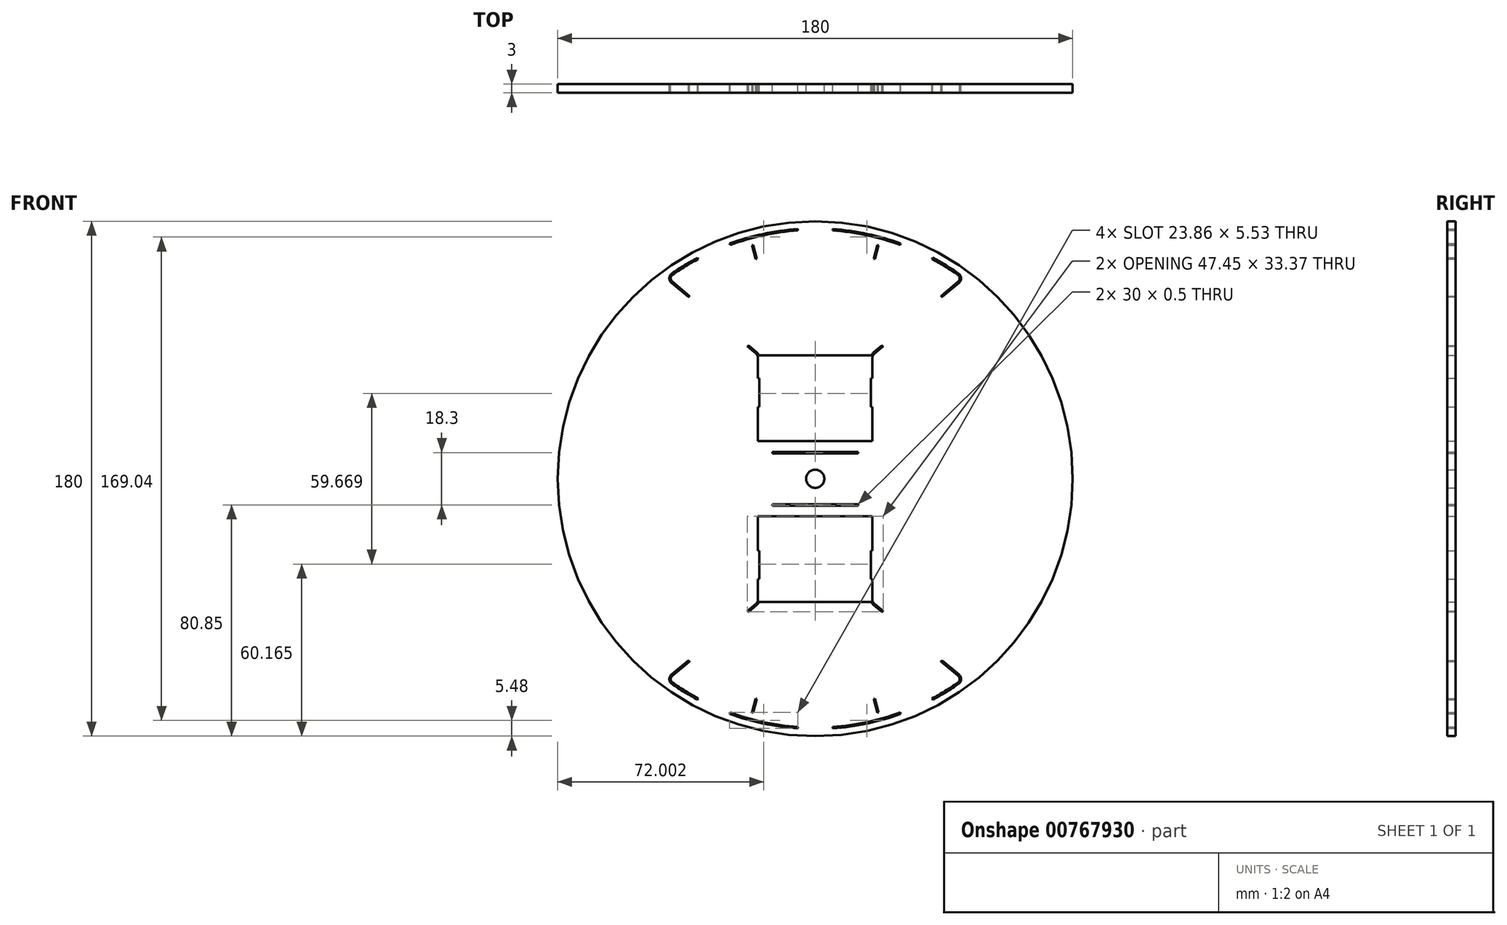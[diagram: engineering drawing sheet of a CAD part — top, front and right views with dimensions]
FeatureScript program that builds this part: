
annotation { "Feature Type Name" : "Feature", "Feature Type Description" : "" }
export const myFeature = defineFeature(function(context is Context, id is Id, definition is map)
    precondition{}
    {
        {
            var Q0;
            Q0=qCreatedBy(makeId("Front.planeOp"),FACE);
            var sketch = newSketch(context, id + "F0", { "sketchPlane" : qUnion([Q0])});
            skCircle(sketch, "E0", {"center": v(0, 0) * mm, "radius": 90 * mm});
            skCircle(sketch, "E1", {"center": v(0, 0) * mm, "radius": 3.17 * mm});
            skLineSegment(sketch, "E2", {"start": v(90, 0) * mm, "end": v(-90, 0) * mm, "construction": true});
            skArc(sketch, "E3", {"start": v(-50.13, -71.72) * mm, "mid": v(-45.69, -74.63) * mm, "end": v(-41.08, -77.26) * mm});
            skLineSegment(sketch, "E4", {"start": v(-20.71, -43.75) * mm, "end": v(-23.72, -46.27) * mm});
            skLineSegment(sketch, "E5", {"start": v(-20, -42.22) * mm, "end": v(-20, -35.15) * mm});
            skLineSegment(sketch, "E6", {"start": v(-18, -13.15) * mm, "end": v(-7.5, -13.15) * mm});
            skLineSegment(sketch, "E7", {"start": v(20, -15.15) * mm, "end": v(20, -25.15) * mm});
            skLineSegment(sketch, "E8.MirrorCS", {"start": v(20.71, -43.75) * mm, "end": v(23.72, -46.27) * mm});
            skPoint(sketch, "E9.visualSharp", {"position": v(-52.23, -70.2) * mm});
            skArc(sketch, "E9.filletArc", {"start": v(-50.27, -68.55) * mm, "mid": v(-50.98, -70.17) * mm, "end": v(-50.13, -71.72) * mm});
            skPoint(sketch, "E10.visualSharp", {"position": v(52.23, -70.2) * mm});
            skArc(sketch, "E10.filletArc", {"start": v(50.13, -71.72) * mm, "mid": v(50.98, -70.17) * mm, "end": v(50.27, -68.55) * mm});
            skPoint(sketch, "E11.visualSharp", {"position": v(-20, -43.15) * mm});
            skArc(sketch, "E11.filletArc", {"start": v(-20.71, -43.75) * mm, "mid": v(-20.19, -43.06) * mm, "end": v(-20, -42.22) * mm});
            skPoint(sketch, "E12.visualSharp", {"position": v(20, -43.15) * mm});
            skArc(sketch, "E12.filletArc", {"start": v(20, -42.22) * mm, "mid": v(20.19, -43.06) * mm, "end": v(20.71, -43.75) * mm});
            skArc(sketch, "E13.1", {"start": v(-20.4, -44.13) * mm, "mid": v(-19.98, -43.69) * mm, "end": v(-19.68, -43.15) * mm});
            skLineSegment(sketch, "E13.3", {"start": v(-20.4, -44.13) * mm, "end": v(-23.24, -46.52) * mm});
            skArc(sketch, "E13.5", {"start": v(19.68, -43.15) * mm, "mid": v(19.98, -43.69) * mm, "end": v(20.4, -44.13) * mm});
            skLineSegment(sketch, "E13.6", {"start": v(20.4, -44.13) * mm, "end": v(23.24, -46.52) * mm});
            skArc(sketch, "E13.7", {"start": v(-49.84, -71.3) * mm, "mid": v(-45.43, -74.2) * mm, "end": v(-40.84, -76.82) * mm});
            skPoint(sketch, "E14.visualSharp", {"position": v(-51.43, -70.17) * mm});
            skArc(sketch, "E14.filletArc", {"start": v(-49.95, -68.93) * mm, "mid": v(-50.48, -70.15) * mm, "end": v(-49.84, -71.3) * mm});
            skPoint(sketch, "E15.visualSharp", {"position": v(51.43, -70.17) * mm});
            skArc(sketch, "E15.filletArc", {"start": v(49.84, -71.3) * mm, "mid": v(50.48, -70.15) * mm, "end": v(49.95, -68.93) * mm});
            skLineSegment(sketch, "E16.1.0", {"start": v(-20.4, -76.94) * mm, "end": v(-21.7, -81.77) * mm});
            skLineSegment(sketch, "E16.1.1", {"start": v(-20.8, -76.84) * mm, "end": v(-22.09, -81.67) * mm});
            skPoint(sketch, "E16.1.2", {"position": v(-21.25, -79.3) * mm});
            skLineSegment(sketch, "E16.1.3", {"start": v(-20.4, -76.94) * mm, "end": v(-20.8, -76.84) * mm});
            skLineSegment(sketch, "E16.1.4", {"start": v(-21.7, -81.77) * mm, "end": v(-22.09, -81.67) * mm});
            skLineSegment(sketch, "E17.MirrorCS", {"start": v(21.7, -81.77) * mm, "end": v(22.09, -81.67) * mm});
            skLineSegment(sketch, "E18.MirrorCS", {"start": v(20.4, -76.94) * mm, "end": v(20.8, -76.84) * mm});
            skPoint(sketch, "E19.MirrorP", {"position": v(21.25, -79.3) * mm});
            skLineSegment(sketch, "E20.MirrorCS", {"start": v(20.8, -76.84) * mm, "end": v(22.09, -81.67) * mm});
            skLineSegment(sketch, "E21.MirrorCS", {"start": v(20.4, -76.94) * mm, "end": v(21.7, -81.77) * mm});
            skLineSegment(sketch, "E22.trimOffspring", {"start": v(-43.9, -63.86) * mm, "end": v(-49.95, -68.93) * mm});
            skLineSegment(sketch, "E23.trimOffspring", {"start": v(-44.33, -63.57) * mm, "end": v(-50.27, -68.55) * mm});
            skLineSegment(sketch, "E24.trimOffspring", {"start": v(43.9, -63.86) * mm, "end": v(49.95, -68.93) * mm});
            skLineSegment(sketch, "E25.trimOffspring", {"start": v(44.33, -63.57) * mm, "end": v(50.27, -68.55) * mm});
            skLineSegment(sketch, "E26", {"start": v(-20, -25.15) * mm, "end": v(-19.5, -25.15) * mm});
            skLineSegment(sketch, "E27", {"start": v(-20, -35.15) * mm, "end": v(-19.5, -35.15) * mm});
            skLineSegment(sketch, "E28.MirrorCS", {"start": v(20, -25.15) * mm, "end": v(19.5, -25.15) * mm});
            skLineSegment(sketch, "E29.MirrorCS", {"start": v(20, -35.15) * mm, "end": v(19.5, -35.15) * mm});
            skLineSegment(sketch, "E30.trimOffspring", {"start": v(-20, -25.15) * mm, "end": v(-20, -15.15) * mm});
            skLineSegment(sketch, "E31.trimOffspring", {"start": v(7.5, -13.15) * mm, "end": v(18, -13.15) * mm});
            skLineSegment(sketch, "E32.trimOffspring", {"start": v(20, -35.15) * mm, "end": v(20, -42.22) * mm});
            skLineSegment(sketch, "E33.trimOffspring", {"start": v(-29.76, -81.75) * mm, "end": v(-29.93, -82.22) * mm});
            skLineSegment(sketch, "E34.trimOffspring", {"start": v(-40.84, -76.82) * mm, "end": v(-41.08, -77.26) * mm});
            skLineSegment(sketch, "E35.trimOffspring", {"start": v(-6.07, -86.79) * mm, "end": v(-6.1, -87.29) * mm});
            skLineSegment(sketch, "E36.trimOffspring", {"start": v(6.07, -86.79) * mm, "end": v(6.1, -87.29) * mm});
            skLineSegment(sketch, "E37.MirrorCS", {"start": v(29.76, -81.75) * mm, "end": v(29.93, -82.22) * mm});
            skLineSegment(sketch, "E38.MirrorCS", {"start": v(40.84, -76.82) * mm, "end": v(41.08, -77.26) * mm});
            skArc(sketch, "E39.trimOffspring", {"start": v(-29.76, -81.75) * mm, "mid": v(-18.09, -85.1) * mm, "end": v(-6.07, -86.79) * mm});
            skArc(sketch, "E40.trimOffspring", {"start": v(-29.93, -82.22) * mm, "mid": v(-18.2, -85.59) * mm, "end": v(-6.1, -87.29) * mm});
            skArc(sketch, "E41.trimOffspring", {"start": v(6.07, -86.79) * mm, "mid": v(18.09, -85.1) * mm, "end": v(29.76, -81.75) * mm});
            skArc(sketch, "E42.trimOffspring", {"start": v(6.1, -87.29) * mm, "mid": v(18.2, -85.59) * mm, "end": v(29.93, -82.22) * mm});
            skArc(sketch, "E43.trimOffspring", {"start": v(41.08, -77.26) * mm, "mid": v(45.69, -74.63) * mm, "end": v(50.13, -71.72) * mm});
            skArc(sketch, "E44.trimOffspring", {"start": v(40.84, -76.82) * mm, "mid": v(45.43, -74.2) * mm, "end": v(49.84, -71.3) * mm});
            skLineSegment(sketch, "E45", {"start": v(-19.68, -43.15) * mm, "end": v(19.68, -43.15) * mm});
            skArc(sketch, "E46", {"start": v(-23.24, -46.52) * mm, "mid": v(-23.48, -46.4) * mm, "end": v(-23.72, -46.27) * mm});
            skArc(sketch, "E47", {"start": v(-43.9, -63.86) * mm, "mid": v(-44.12, -63.72) * mm, "end": v(-44.33, -63.57) * mm});
            skArc(sketch, "E48", {"start": v(23.24, -46.52) * mm, "mid": v(23.48, -46.4) * mm, "end": v(23.72, -46.27) * mm});
            skArc(sketch, "E49", {"start": v(43.9, -63.86) * mm, "mid": v(44.12, -63.72) * mm, "end": v(44.33, -63.57) * mm});
            skLineSegment(sketch, "E50", {"start": v(-19.5, -35.15) * mm, "end": v(-19.5, -25.15) * mm});
            skLineSegment(sketch, "E51", {"start": v(19.5, -35.15) * mm, "end": v(19.5, -25.15) * mm});
            skLineSegment(sketch, "E52", {"start": v(18, -13.15) * mm, "end": v(20, -13.15) * mm});
            skLineSegment(sketch, "E53", {"start": v(20, -13.15) * mm, "end": v(20, -15.15) * mm});
            skLineSegment(sketch, "E54", {"start": v(-20, -15.15) * mm, "end": v(-20, -13.15) * mm});
            skLineSegment(sketch, "E55", {"start": v(-20, -13.15) * mm, "end": v(-18, -13.15) * mm});
            skLineSegment(sketch, "E56", {"start": v(-7.5, -13.15) * mm, "end": v(7.5, -13.15) * mm});
            skLineSegment(sketch, "E57.MirrorCS", {"start": v(20.4, 44.13) * mm, "end": v(23.24, 46.52) * mm});
            skLineSegment(sketch, "E58.MirrorCS", {"start": v(-29.76, 81.75) * mm, "end": v(-29.93, 82.22) * mm});
            skLineSegment(sketch, "E59.MirrorCS", {"start": v(20.71, 43.75) * mm, "end": v(23.72, 46.27) * mm});
            skArc(sketch, "E60.MirrorCS", {"start": v(-43.9, 63.86) * mm, "mid": v(-44.12, 63.72) * mm, "end": v(-44.33, 63.57) * mm});
            skArc(sketch, "E61.MirrorCS", {"start": v(-49.95, 68.93) * mm, "mid": v(-50.48, 70.15) * mm, "end": v(-49.84, 71.3) * mm});
            skLineSegment(sketch, "E62.MirrorCS", {"start": v(-40.84, 76.82) * mm, "end": v(-41.08, 77.26) * mm});
            skArc(sketch, "E63.MirrorCS", {"start": v(-50.27, 68.55) * mm, "mid": v(-50.98, 70.17) * mm, "end": v(-50.13, 71.72) * mm});
            skArc(sketch, "E64.MirrorCS", {"start": v(43.9, 63.86) * mm, "mid": v(44.12, 63.72) * mm, "end": v(44.33, 63.57) * mm});
            skArc(sketch, "E65.MirrorCS", {"start": v(23.24, 46.52) * mm, "mid": v(23.48, 46.4) * mm, "end": v(23.72, 46.27) * mm});
            skLineSegment(sketch, "E66.MirrorCS", {"start": v(43.9, 63.86) * mm, "end": v(49.95, 68.93) * mm});
            skArc(sketch, "E67.MirrorCS", {"start": v(19.68, 43.15) * mm, "mid": v(19.98, 43.69) * mm, "end": v(20.4, 44.13) * mm});
            skLineSegment(sketch, "E68.MirrorCS", {"start": v(40.84, 76.82) * mm, "end": v(41.08, 77.26) * mm});
            skArc(sketch, "E69.MirrorCS", {"start": v(49.84, 71.3) * mm, "mid": v(50.48, 70.15) * mm, "end": v(49.95, 68.93) * mm});
            skLineSegment(sketch, "E70.MirrorCS", {"start": v(29.76, 81.75) * mm, "end": v(29.93, 82.22) * mm});
            skArc(sketch, "E71.MirrorCS", {"start": v(20, 42.22) * mm, "mid": v(20.19, 43.06) * mm, "end": v(20.71, 43.75) * mm});
            skArc(sketch, "E72.MirrorCS", {"start": v(50.13, 71.72) * mm, "mid": v(50.98, 70.17) * mm, "end": v(50.27, 68.55) * mm});
            skLineSegment(sketch, "E73.MirrorCS", {"start": v(-21.7, 81.77) * mm, "end": v(-22.09, 81.67) * mm});
            skLineSegment(sketch, "E74.MirrorCS", {"start": v(20.4, 76.94) * mm, "end": v(20.8, 76.84) * mm});
            skLineSegment(sketch, "E75.MirrorCS", {"start": v(-20.71, 43.75) * mm, "end": v(-23.72, 46.27) * mm});
            skArc(sketch, "E76.MirrorCS", {"start": v(-23.24, 46.52) * mm, "mid": v(-23.48, 46.4) * mm, "end": v(-23.72, 46.27) * mm});
            skLineSegment(sketch, "E77.MirrorCS", {"start": v(20, 13.15) * mm, "end": v(20, 15.15) * mm});
            skArc(sketch, "E78.MirrorCS", {"start": v(-20.71, 43.75) * mm, "mid": v(-20.19, 43.06) * mm, "end": v(-20, 42.22) * mm});
            skArc(sketch, "E79.MirrorCS", {"start": v(-20.4, 44.13) * mm, "mid": v(-19.98, 43.69) * mm, "end": v(-19.68, 43.15) * mm});
            skLineSegment(sketch, "E80.MirrorCS", {"start": v(18, 13.15) * mm, "end": v(20, 13.15) * mm});
            skLineSegment(sketch, "E81.MirrorCS", {"start": v(-6.07, 86.79) * mm, "end": v(-6.1, 87.29) * mm});
            skLineSegment(sketch, "E82.MirrorCS", {"start": v(6.07, 86.79) * mm, "end": v(6.1, 87.29) * mm});
            skLineSegment(sketch, "E83.MirrorCS", {"start": v(-20, 25.15) * mm, "end": v(-19.5, 25.15) * mm});
            skLineSegment(sketch, "E84.MirrorCS", {"start": v(21.7, 81.77) * mm, "end": v(22.09, 81.67) * mm});
            skLineSegment(sketch, "E85.MirrorCS", {"start": v(-20.4, 76.94) * mm, "end": v(-20.8, 76.84) * mm});
            skLineSegment(sketch, "E86.MirrorCS", {"start": v(20.4, 76.94) * mm, "end": v(21.7, 81.77) * mm});
            skLineSegment(sketch, "E87.MirrorCS", {"start": v(-20, 35.15) * mm, "end": v(-19.5, 35.15) * mm});
            skLineSegment(sketch, "E88.MirrorCS", {"start": v(-20, 15.15) * mm, "end": v(-20, 13.15) * mm});
            skLineSegment(sketch, "E89.MirrorCS", {"start": v(20, 35.15) * mm, "end": v(19.5, 35.15) * mm});
            skLineSegment(sketch, "E90.MirrorCS", {"start": v(-20, 13.15) * mm, "end": v(-18, 13.15) * mm});
            skLineSegment(sketch, "E91.MirrorCS", {"start": v(-20.4, 76.94) * mm, "end": v(-21.7, 81.77) * mm});
            skLineSegment(sketch, "E92.MirrorCS", {"start": v(20.8, 76.84) * mm, "end": v(22.09, 81.67) * mm});
            skLineSegment(sketch, "E93.MirrorCS", {"start": v(-20.8, 76.84) * mm, "end": v(-22.09, 81.67) * mm});
            skLineSegment(sketch, "E94.MirrorCS", {"start": v(20, 25.15) * mm, "end": v(19.5, 25.15) * mm});
            skLineSegment(sketch, "E95.MirrorCS", {"start": v(-20.4, 44.13) * mm, "end": v(-23.24, 46.52) * mm});
            skArc(sketch, "E96.MirrorCS", {"start": v(-49.84, 71.3) * mm, "mid": v(-45.43, 74.2) * mm, "end": v(-40.84, 76.82) * mm});
            skLineSegment(sketch, "E97.MirrorCS", {"start": v(-20, 42.22) * mm, "end": v(-20, 35.15) * mm});
            skPoint(sketch, "E98.MirrorP", {"position": v(51.43, 70.17) * mm});
            skLineSegment(sketch, "E99.MirrorCS", {"start": v(-43.9, 63.86) * mm, "end": v(-49.95, 68.93) * mm});
            skLineSegment(sketch, "E100.MirrorCS", {"start": v(20, 35.15) * mm, "end": v(20, 42.22) * mm});
            skPoint(sketch, "E101.MirrorP", {"position": v(-52.23, 70.2) * mm});
            skArc(sketch, "E102.MirrorCS", {"start": v(40.84, 76.82) * mm, "mid": v(45.43, 74.2) * mm, "end": v(49.84, 71.3) * mm});
            skLineSegment(sketch, "E103.MirrorCS", {"start": v(-7.5, 13.15) * mm, "end": v(7.5, 13.15) * mm});
            skLineSegment(sketch, "E104.MirrorCS", {"start": v(-19.68, 43.15) * mm, "end": v(19.68, 43.15) * mm});
            skLineSegment(sketch, "E105.MirrorCS", {"start": v(19.5, 35.15) * mm, "end": v(19.5, 25.15) * mm});
            skLineSegment(sketch, "E106.MirrorCS", {"start": v(7.5, 13.15) * mm, "end": v(18, 13.15) * mm});
            skArc(sketch, "E107.MirrorCS", {"start": v(-29.76, 81.75) * mm, "mid": v(-18.09, 85.1) * mm, "end": v(-6.07, 86.79) * mm});
            skArc(sketch, "E108.MirrorCS", {"start": v(-29.93, 82.22) * mm, "mid": v(-18.2, 85.59) * mm, "end": v(-6.1, 87.29) * mm});
            skLineSegment(sketch, "E109.MirrorCS", {"start": v(-44.33, 63.57) * mm, "end": v(-50.27, 68.55) * mm});
            skPoint(sketch, "E110.MirrorP", {"position": v(21.25, 79.3) * mm});
            skArc(sketch, "E111.MirrorCS", {"start": v(6.07, 86.79) * mm, "mid": v(18.09, 85.1) * mm, "end": v(29.76, 81.75) * mm});
            skArc(sketch, "E112.MirrorCS", {"start": v(6.1, 87.29) * mm, "mid": v(18.2, 85.59) * mm, "end": v(29.93, 82.22) * mm});
            skPoint(sketch, "E113.MirrorP", {"position": v(-21.25, 79.3) * mm});
            skLineSegment(sketch, "E114.MirrorCS", {"start": v(44.33, 63.57) * mm, "end": v(50.27, 68.55) * mm});
            skPoint(sketch, "E115.MirrorP", {"position": v(-20, 43.15) * mm});
            skPoint(sketch, "E116.MirrorP", {"position": v(52.23, 70.2) * mm});
            skLineSegment(sketch, "E117.MirrorCS", {"start": v(20, 15.15) * mm, "end": v(20, 25.15) * mm});
            skArc(sketch, "E118.MirrorCS", {"start": v(-50.13, 71.72) * mm, "mid": v(-45.69, 74.63) * mm, "end": v(-41.08, 77.26) * mm});
            skPoint(sketch, "E119.MirrorP", {"position": v(20, 43.15) * mm});
            skLineSegment(sketch, "E120.MirrorCS", {"start": v(-19.5, 35.15) * mm, "end": v(-19.5, 25.15) * mm});
            skLineSegment(sketch, "E121.MirrorCS", {"start": v(-18, 13.15) * mm, "end": v(-7.5, 13.15) * mm});
            skLineSegment(sketch, "E122.MirrorCS", {"start": v(-20, 25.15) * mm, "end": v(-20, 15.15) * mm});
            skArc(sketch, "E123.MirrorCS", {"start": v(41.08, 77.26) * mm, "mid": v(45.69, 74.63) * mm, "end": v(50.13, 71.72) * mm});
            skPoint(sketch, "E124.MirrorP", {"position": v(-51.43, 70.17) * mm});
            skLineSegment(sketch, "E125.bottom", {"start": v(15, 9.4) * mm, "end": v(-15, 9.4) * mm});
            skLineSegment(sketch, "E125.top", {"start": v(15, 8.9) * mm, "end": v(-15, 8.9) * mm});
            skLineSegment(sketch, "E125.left", {"start": v(15, 9.4) * mm, "end": v(15, 8.9) * mm});
            skLineSegment(sketch, "E125.right", {"start": v(-15, 9.4) * mm, "end": v(-15, 8.9) * mm});
            skPoint(sketch, "E125.middle", {"position": v(0, 9.15) * mm});
            skLineSegment(sketch, "E126.MirrorCS", {"start": v(-15, -9.4) * mm, "end": v(-15, -8.9) * mm});
            skLineSegment(sketch, "E127.MirrorCS", {"start": v(15, -9.4) * mm, "end": v(15, -8.9) * mm});
            skLineSegment(sketch, "E128.MirrorCS", {"start": v(15, -8.9) * mm, "end": v(-15, -8.9) * mm});
            skPoint(sketch, "E129.MirrorP", {"position": v(0, -9.15) * mm});
            skLineSegment(sketch, "E130.MirrorCS", {"start": v(15, -9.4) * mm, "end": v(-15, -9.4) * mm});
            skSolve(sketch);
        }
        {
            var Q0;
            Q0=makeQuery(id+"F0.imprint","IMPRINT",FACE,{"disambiguationData":[TD([[makeQuery(id+"F0.imprint","IMPRINT",EDGE,{"derivedFrom":sQuery(id+"F0.wireOp",EDGE,"E0")}),1.0]])]});
            extrude(context, id + "F1", {"entities" : qUnion([Q0]), "depth" : 3 * mm, "offsetDistance" : 25 * mm});
        }
    });
